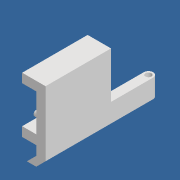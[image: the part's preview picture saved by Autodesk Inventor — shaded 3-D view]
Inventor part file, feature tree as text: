
AUTODESK INVENTOR PART (.ipt)
format: ipt  version: 2020 (Build 240168000, 168)  size: 220,160 bytes
history: native  units: mm
features: sketch x10, extrude x9, chamfer x2, split x1, fillet x1
ambient origin geometry x8: Origin, YZ Plane, XZ Plane, XY Plane, X Axis, Y Axis, Z Axis, Center Point
bodies: Solid1 (feature_tree)
feature tree (23):
  extrude  "Extrusion1"  Depth=56.0mm
  extrude  "Extrusion2"  Depth=40.0mm
  extrude  "Extrusion3"  Depth=7.8mm
  extrude  "Extrusion4"  Depth=4.6mm
  sketch  "Sketch14"  dims[d10=4.6mm d11=16.0mm]
  extrude  "Extrusion7"  Depth=16.0mm
  extrude  "Extrusion8"  Depth=12.0mm TaperAngle=0.0deg
  chamfer  "Chamfer1"  Distance=26.0mm
  chamfer  "Chamfer2"  Distance=24.0mm
  split  "Split2"
  extrude  "Extrusion9"  Depth=8.0mm
  extrude  "Extrusion13"  Depth=8.0mm
  extrude  "Extrusion14"  Depth=8.0mm
  fillet  "Fillet2"  Radius=8.0mm
  sketch  "Sketch1"  dims[d0=39.6mm d1=56.0mm]
  sketch  "Sketch2"  dims[d2=40.0mm d3=0.0mm d4=24.4mm]
  sketch  "Sketch3"  dims[d5=31.8mm d6=7.8mm]
  sketch  "Sketch4"  dims[d7=64.0mm d8=0.0mm d9=4.6mm]
  sketch  "Sketch15"  dims[d12=12.0mm d13=26.0mm d14=0.0mm]
  sketch  "Sketch16"  dims[d15=24.0mm]
  sketch  "Sketch17"  dims[d16=8.0mm d17=26.0mm d18=0.0mm d35=24.0mm d36=0.0mm]
  sketch  "Sketch22"  dims[d37=24.0mm d38=8.0mm]
  sketch  "Sketch23"  dims[d39=8.0mm d40=8.0mm d41=8.0mm d42=8.0mm d43=16.0mm d44=0.0mm d45=0.0mm d46=8.0mm d47=2.0mm d48=45.0deg d49=8.0mm d50=2.0mm d51=45.0deg d52=5.0mm d53=5.0mm d55=5.0mm d56=5.0mm d57=5.0mm d58=5.0mm d59=16.0mm d60=16.0mm d61=40.0mm d62=4.0mm d63=12.0mm d64=8.0mm d65=0.0mm d82=8.0mm d83=16.0mm d84=40.0mm d85=0.0mm d86=5.0mm d87=4.0mm d88=4.0mm d89=0.0mm d90=0.0mm d91=4.0mm d92=14.3117mm d93=0.75mm d94=20.594885mm d95=0.0625mm d96=0.75mm d97=0.375mm]
